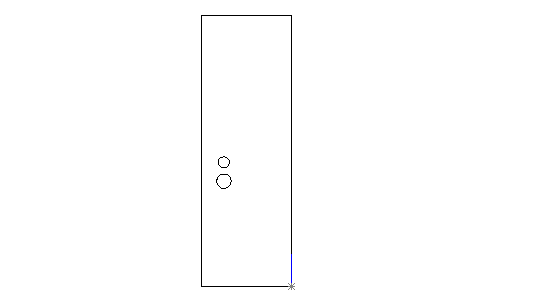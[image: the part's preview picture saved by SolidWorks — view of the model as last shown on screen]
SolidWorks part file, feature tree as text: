
SOLIDWORKS PART (.sldprt)
format: sldprt  version: not decoded by parser v0  size: 272,384 bytes
history: native  units: mm
features: sketch x5, extrude x4, cut_extrude x1 (+11 scaffold rows collapsed)
feature tree (21):
  scaffold x11  (default folders/planes/origin — collapsed)
  sketch  "Sketch1"  dims[D1=76.2mm D2=76.2mm]
  extrude  "Extrude1"  Depth=12.7mm
  sketch  "Sketch2"  dims[D1=7.874mm D2=7.874mm D3=30.48mm D4=22.225mm D5=15.875mm]
  extrude  "Extrude2"  Depth=6.35mm
  sketch  "Sketch3"  dims[D1=6.35mm]
  extrude  "Extrude3"  Depth=12.7mm
  sketch  "Sketch4"  dims[D1=6.35mm]
  extrude  "Extrude4"  Depth=12.7mm
  sketch  "Sketch6"  dims[D1=3.175mm D4=4.1275mm D2=34.925mm D3=6.35mm D5=~29.609584mm]
  cut_extrude  "Cut-Extrude1"  [1 undecoded]
decode coverage: 9 of 10 modeling features carry decoded parameters
note: ~ marks probable driven/reference dimensions
note: 1 parameter value undecoded
note: suppression state not decoded; provenance and decode notes live in map.json
